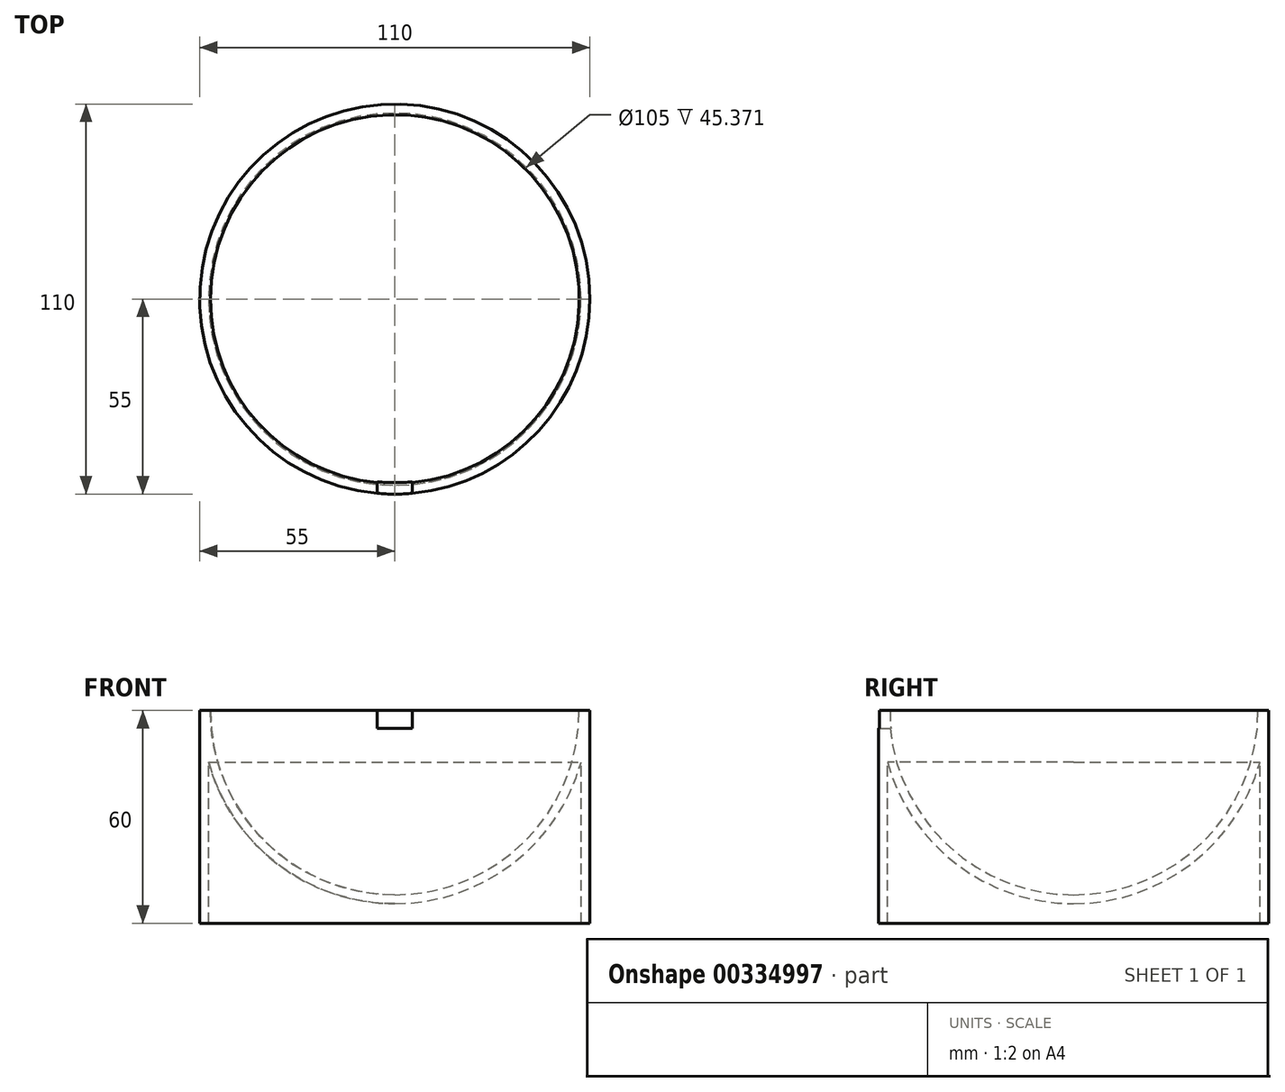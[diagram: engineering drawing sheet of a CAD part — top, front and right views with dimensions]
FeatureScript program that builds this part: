
annotation { "Feature Type Name" : "Feature", "Feature Type Description" : "" }
export const myFeature = defineFeature(function(context is Context, id is Id, definition is map)
    precondition{}
    {
        {
            var Q0;
            Q0=qCreatedBy(makeId("Front.planeOp"),FACE);
            var sketch = newSketch(context, id + "F0", { "sketchPlane" : qUnion([Q0])});
            skArc(sketch, "E0", {"start": v(-52, 0) * mm, "mid": v(-36.77, -36.77) * mm, "end": v(0, -52) * mm});
            skLineSegment(sketch, "E1.bottom", {"start": v(-52, 0) * mm, "end": v(-55, 0) * mm});
            skLineSegment(sketch, "E1.top", {"start": v(0, -60) * mm, "end": v(-55, -60) * mm});
            skLineSegment(sketch, "E1.left", {"start": v(0, -52) * mm, "end": v(0, -60) * mm});
            skLineSegment(sketch, "E1.right", {"start": v(-55, 0) * mm, "end": v(-55, -60) * mm});
            skSolve(sketch);
        }
        {
            var Q0;
            Q0=makeQuery(id+"F0.imprint","IMPRINT",FACE,{"disambiguationData":[TD([[makeQuery(id+"F0.imprint","IMPRINT",EDGE,{"derivedFrom":sQuery(id+"F0.wireOp",EDGE,"E0")}),-1.0]])]});
            var Q1;
            Q1=sQuery(id+"F0.wireOp",EDGE,"E1.left");
            revolve(context, id + "F1", {"entities" : qUnion([Q0]), "axis" : qUnion([Q1]), "revolveType" : RevolveType.FULL});
        }
        {
            var Q0;
            Q0=makeQuery(id+"F1.opRevolve","SWEPT_FACE",FACE,{"disambiguationData":[OSD([sQuery(id+"F0.wireOp",EDGE,"E1.top")])]});
            shell(context, id + "F2", {"entities" : qUnion([Q0]), "thickness" : 2.5 * mm});
        }
        {
            var Q0;
            Q0=qCreatedBy(makeId("Front.planeOp"),FACE);
            var sketch = newSketch(context, id + "F3", { "sketchPlane" : qUnion([Q0])});
            skLineSegment(sketch, "E2.bottom", {"start": v(-5, 0) * mm, "end": v(5, 0) * mm});
            skLineSegment(sketch, "E2.top", {"start": v(-5, -5) * mm, "end": v(5, -5) * mm});
            skLineSegment(sketch, "E2.left", {"start": v(-5, 0) * mm, "end": v(-5, -5) * mm});
            skLineSegment(sketch, "E2.right", {"start": v(5, 0) * mm, "end": v(5, -5) * mm});
            skPoint(sketch, "E2.middle", {"position": v(0, -2.5) * mm});
            skSolve(sketch);
        }
        {
            var Q0;
            Q0=makeQuery(id+"F3.imprint","IMPRINT",FACE,{"disambiguationData":[TD([[makeQuery(id+"F3.imprint","IMPRINT",EDGE,{"derivedFrom":sQuery(id+"F3.wireOp",EDGE,"E2.bottom")}),-1.0]])]});
            extrude(context, id + "F4", {"entities" : qUnion([Q0]), "operationType" : NewBodyOperationType.REMOVE, "depth" : 55 * mm});
        }
    });
